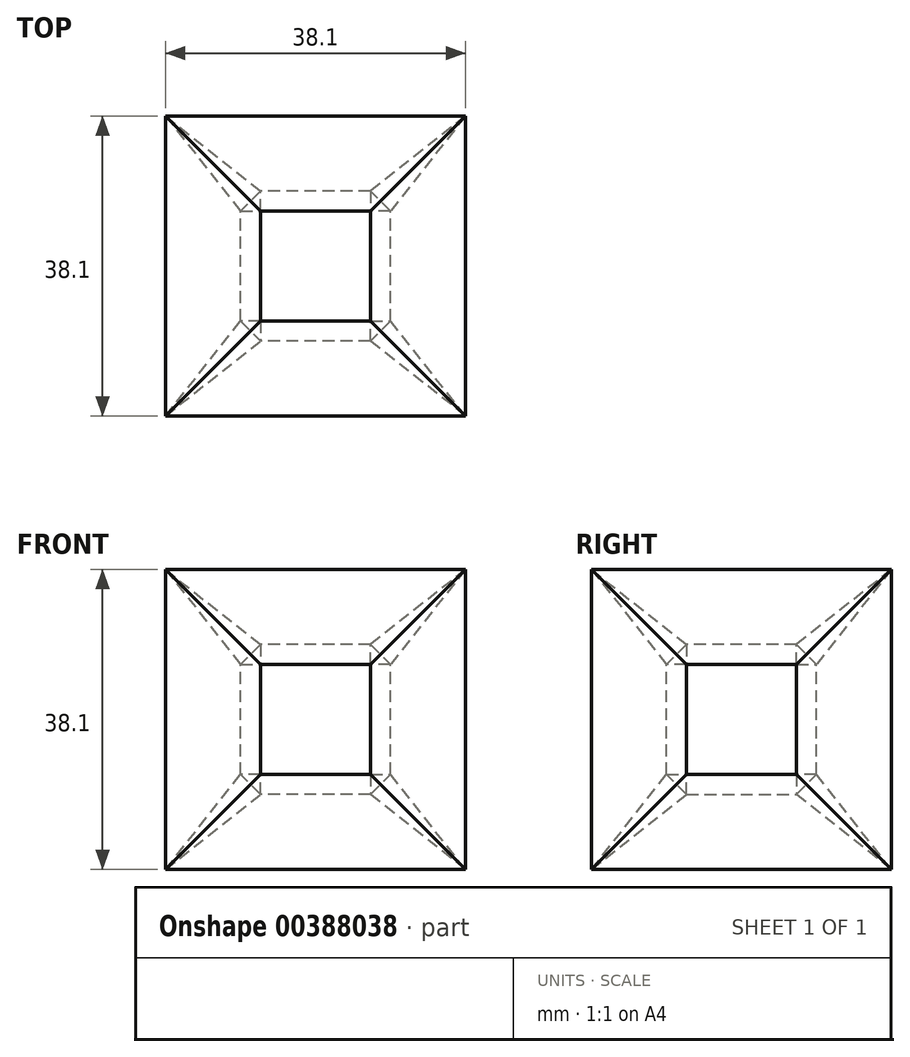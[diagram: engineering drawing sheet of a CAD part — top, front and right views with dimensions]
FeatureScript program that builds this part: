
annotation { "Feature Type Name" : "Feature", "Feature Type Description" : "" }
export const myFeature = defineFeature(function(context is Context, id is Id, definition is map)
    precondition{}
    {
        {
            assignVariable(context, id + "F0", {"name" : "Outer", "anyValue" : 38.1 * mm});
        }
        {
            assignVariable(context, id + "F1", {"name" : "Inner", "anyValue" : 19.05 * mm});
        }
        {
            assignVariable(context, id + "F2", {"name" : "Chamfer", "anyValue" : 2.54 * mm});
        }
        {
            var Q0;
            Q0=qCreatedBy(makeId("Top.planeOp"),FACE);
            var sketch = newSketch(context, id + "F3", { "sketchPlane" : qUnion([Q0])});
            skLineSegment(sketch, "E0.bottom", {"start": v(9.53, 9.53) * mm, "end": v(-9.52, 9.53) * mm});
            skLineSegment(sketch, "E0.top", {"start": v(9.53, -9.53) * mm, "end": v(-9.53, -9.53) * mm});
            skLineSegment(sketch, "E0.left", {"start": v(9.53, 9.53) * mm, "end": v(9.53, -9.53) * mm});
            skLineSegment(sketch, "E0.right", {"start": v(-9.52, 9.53) * mm, "end": v(-9.52, -9.53) * mm});
            skPoint(sketch, "E0.middle", {"position": v(0, 0) * mm});
            skSolve(sketch);
        }
        {
            var Q0;
            Q0=makeQuery(id+"F3.imprint","IMPRINT",FACE,{"disambiguationData":[TD([[makeQuery(id+"F3.imprint","IMPRINT",EDGE,{"derivedFrom":sQuery(id+"F3.wireOp",EDGE,"E0.bottom")}),1.0]])]});
            extrude(context, id + "F4", {"entities" : qUnion([Q0]), "endBound" : BoundingType.SYMMETRIC, "depth" : getVariable(context, 'Inner')});
        }
        {
            var Q0;
            Q0=makeQuery(id+"F4.opExtrude","CAP_EDGE",EDGE,{"disambiguationData":[OSD([sQuery(id+"F3.wireOp",EDGE,"E0.top")])],"isStart":true});
            var Q1;
            Q1=makeQuery(id+"F4.opExtrude","SWEPT_EDGE",EDGE,{"disambiguationData":[OSD([sQuery(id+"F3.wireOp",EDGE,"E0.top"),sQuery(id+"F3.wireOp",EDGE,"E0.left")])]});
            var Q2;
            Q2=makeQuery(id+"F4.opExtrude","SWEPT_EDGE",EDGE,{"disambiguationData":[OSD([sQuery(id+"F3.wireOp",EDGE,"E0.bottom"),sQuery(id+"F3.wireOp",EDGE,"E0.left")])]});
            var Q3;
            Q3=makeQuery(id+"F4.opExtrude","CAP_EDGE",EDGE,{"disambiguationData":[OSD([sQuery(id+"F3.wireOp",EDGE,"E0.bottom")])],"isStart":false});
            var Q4;
            Q4=makeQuery(id+"F4.opExtrude","SWEPT_EDGE",EDGE,{"disambiguationData":[OSD([sQuery(id+"F3.wireOp",EDGE,"E0.top"),sQuery(id+"F3.wireOp",EDGE,"E0.right")])]});
            var Q5;
            Q5=makeQuery(id+"F4.opExtrude","CAP_EDGE",EDGE,{"disambiguationData":[OSD([sQuery(id+"F3.wireOp",EDGE,"E0.top")])],"isStart":false});
            var Q6;
            Q6=makeQuery(id+"F4.opExtrude","CAP_EDGE",EDGE,{"disambiguationData":[OSD([sQuery(id+"F3.wireOp",EDGE,"E0.left")])],"isStart":true});
            var Q7;
            Q7=makeQuery(id+"F4.opExtrude","CAP_EDGE",EDGE,{"disambiguationData":[OSD([sQuery(id+"F3.wireOp",EDGE,"E0.right")])],"isStart":true});
            var Q8;
            Q8=makeQuery(id+"F4.opExtrude","CAP_EDGE",EDGE,{"disambiguationData":[OSD([sQuery(id+"F3.wireOp",EDGE,"E0.left")])],"isStart":false});
            var Q9;
            Q9=makeQuery(id+"F4.opExtrude","SWEPT_EDGE",EDGE,{"disambiguationData":[OSD([sQuery(id+"F3.wireOp",EDGE,"E0.bottom"),sQuery(id+"F3.wireOp",EDGE,"E0.right")])]});
            var Q10;
            Q10=makeQuery(id+"F4.opExtrude","CAP_EDGE",EDGE,{"disambiguationData":[OSD([sQuery(id+"F3.wireOp",EDGE,"E0.right")])],"isStart":false});
            var Q11;
            Q11=makeQuery(id+"F4.opExtrude","CAP_EDGE",EDGE,{"disambiguationData":[OSD([sQuery(id+"F3.wireOp",EDGE,"E0.bottom")])],"isStart":true});
            chamfer(context, id + "F5", {"entities" : qUnion([Q0, Q1, Q2, Q3, Q4, Q5, Q6, Q7, Q8, Q9, Q10, Q11]), "width" : getVariable(context, 'Chamfer'), "tangentPropagation" : true});
        }
        {
            var Q0;
            Q0=qCreatedBy(makeId("Top.planeOp"),FACE);
            var sketch = newSketch(context, id + "F6", { "sketchPlane" : qUnion([Q0])});
            skLineSegment(sketch, "E1.bottom", {"start": v(19.05, 19.05) * mm, "end": v(-19.05, 19.05) * mm});
            skLineSegment(sketch, "E1.top", {"start": v(19.05, -19.05) * mm, "end": v(-19.05, -19.05) * mm});
            skLineSegment(sketch, "E1.left", {"start": v(19.05, 19.05) * mm, "end": v(19.05, -19.05) * mm});
            skLineSegment(sketch, "E1.right", {"start": v(-19.05, 19.05) * mm, "end": v(-19.05, -19.05) * mm});
            skPoint(sketch, "E1.middle", {"position": v(0, 0) * mm});
            skSolve(sketch);
        }
        {
            var Q0;
            Q0=makeQuery(id+"F6.imprint","IMPRINT",FACE,{"disambiguationData":[TD([[makeQuery(id+"F6.imprint","IMPRINT",EDGE,{"derivedFrom":sQuery(id+"F6.wireOp",EDGE,"E1.bottom")}),1.0]])]});
            extrude(context, id + "F7", {"entities" : qUnion([Q0]), "endBound" : BoundingType.SYMMETRIC, "depth" : getVariable(context, 'Outer')});
        }
        {
            var Q1;
            Q1=makeQuery(id+"F7.opExtrude","SWEPT_FACE",FACE,{"disambiguationData":[OSD([sQuery(id+"F6.wireOp",EDGE,"E1.top")])]});
            var Q2;
            Q2=makeQuery(id+"F4.opExtrude","SWEPT_FACE",FACE,{"disambiguationData":[OSD([sQuery(id+"F3.wireOp",EDGE,"E0.top")])]});
            loft(context, id + "F8", {"operationType" : NewBodyOperationType.REMOVE, "sheetProfilesArray" : [{ "sheetProfileEntities" : qUnion([Q1]) }, { "sheetProfileEntities" : qUnion([Q2]) }]});
        }
        {
            var Q1;
            Q1=makeQuery(id+"F7.opExtrude","CAP_FACE",FACE,{"disambiguationData":[OSD([sQuery(id+"F6.wireOp",EDGE,"E1.bottom"),sQuery(id+"F6.wireOp",EDGE,"E1.top"),sQuery(id+"F6.wireOp",EDGE,"E1.left"),sQuery(id+"F6.wireOp",EDGE,"E1.right")])],"isStart":false});
            var Q2;
            Q2=makeQuery(id+"F4.opExtrude","CAP_FACE",FACE,{"disambiguationData":[OSD([sQuery(id+"F3.wireOp",EDGE,"E0.bottom"),sQuery(id+"F3.wireOp",EDGE,"E0.top"),sQuery(id+"F3.wireOp",EDGE,"E0.left"),sQuery(id+"F3.wireOp",EDGE,"E0.right")])],"isStart":false});
            loft(context, id + "F9", {"operationType" : NewBodyOperationType.REMOVE, "sheetProfilesArray" : [{ "sheetProfileEntities" : qUnion([Q1]) }, { "sheetProfileEntities" : qUnion([Q2]) }]});
        }
        {
            var Q1;
            Q1=makeQuery(id+"F7.opExtrude","SWEPT_FACE",FACE,{"disambiguationData":[OSD([sQuery(id+"F6.wireOp",EDGE,"E1.bottom")])]});
            var Q2;
            Q2=makeQuery(id+"F4.opExtrude","SWEPT_FACE",FACE,{"disambiguationData":[OSD([sQuery(id+"F3.wireOp",EDGE,"E0.bottom")])]});
            loft(context, id + "F10", {"operationType" : NewBodyOperationType.REMOVE, "sheetProfilesArray" : [{ "sheetProfileEntities" : qUnion([Q1]) }, { "sheetProfileEntities" : qUnion([Q2]) }]});
        }
        {
            var Q1;
            Q1=makeQuery(id+"F7.opExtrude","SWEPT_FACE",FACE,{"disambiguationData":[OSD([sQuery(id+"F6.wireOp",EDGE,"E1.left")])]});
            var Q2;
            Q2=makeQuery(id+"F4.opExtrude","SWEPT_FACE",FACE,{"disambiguationData":[OSD([sQuery(id+"F3.wireOp",EDGE,"E0.left")])]});
            loft(context, id + "F11", {"operationType" : NewBodyOperationType.REMOVE, "sheetProfilesArray" : [{ "sheetProfileEntities" : qUnion([Q1]) }, { "sheetProfileEntities" : qUnion([Q2]) }]});
        }
        {
            var Q1;
            Q1=makeQuery(id+"F7.opExtrude","SWEPT_FACE",FACE,{"disambiguationData":[OSD([sQuery(id+"F6.wireOp",EDGE,"E1.right")])]});
            var Q2;
            Q2=makeQuery(id+"F4.opExtrude","SWEPT_FACE",FACE,{"disambiguationData":[OSD([sQuery(id+"F3.wireOp",EDGE,"E0.right")])]});
            loft(context, id + "F12", {"operationType" : NewBodyOperationType.REMOVE, "sheetProfilesArray" : [{ "sheetProfileEntities" : qUnion([Q1]) }, { "sheetProfileEntities" : qUnion([Q2]) }]});
        }
        {
            var Q1;
            Q1=makeQuery(id+"F7.opExtrude","CAP_FACE",FACE,{"disambiguationData":[OSD([sQuery(id+"F6.wireOp",EDGE,"E1.bottom"),sQuery(id+"F6.wireOp",EDGE,"E1.top"),sQuery(id+"F6.wireOp",EDGE,"E1.left"),sQuery(id+"F6.wireOp",EDGE,"E1.right")])],"isStart":true});
            var Q2;
            Q2=makeQuery(id+"F4.opExtrude","CAP_FACE",FACE,{"disambiguationData":[OSD([sQuery(id+"F3.wireOp",EDGE,"E0.bottom"),sQuery(id+"F3.wireOp",EDGE,"E0.top"),sQuery(id+"F3.wireOp",EDGE,"E0.left"),sQuery(id+"F3.wireOp",EDGE,"E0.right")])],"isStart":true});
            loft(context, id + "F13", {"operationType" : NewBodyOperationType.REMOVE, "sheetProfilesArray" : [{ "sheetProfileEntities" : qUnion([Q1]) }, { "sheetProfileEntities" : qUnion([Q2]) }]});
        }
    });
